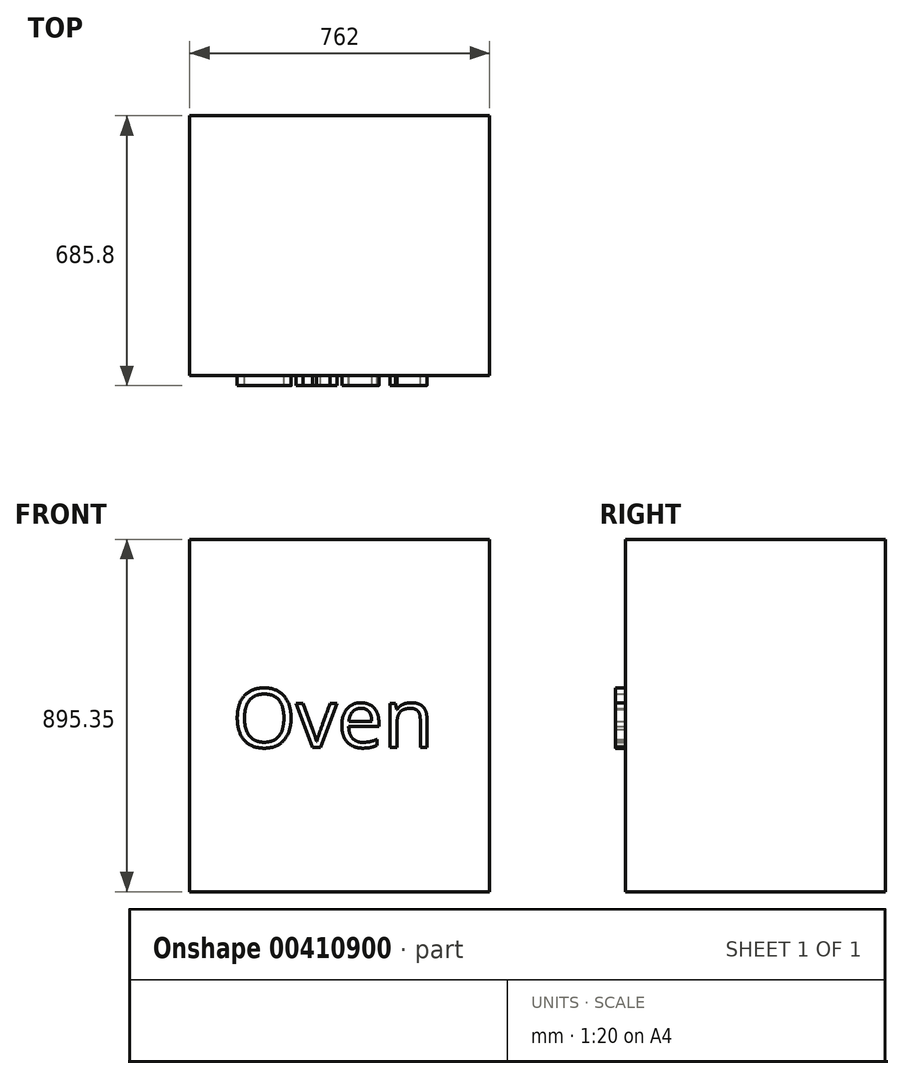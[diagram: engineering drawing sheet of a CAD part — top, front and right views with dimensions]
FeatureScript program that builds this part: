
annotation { "Feature Type Name" : "Feature", "Feature Type Description" : "" }
export const myFeature = defineFeature(function(context is Context, id is Id, definition is map)
    precondition{}
    {
        {
            var Q0;
            Q0=qCreatedBy(makeId("Front.planeOp"),FACE);
            var sketch = newSketch(context, id + "F0", { "sketchPlane" : qUnion([Q0])});
            skLineSegment(sketch, "E0.bottom", {"start": v(-762, 895.35) * mm, "end": v(0, 895.35) * mm});
            skLineSegment(sketch, "E0.top", {"start": v(-762, 0) * mm, "end": v(0, 0) * mm});
            skLineSegment(sketch, "E0.left", {"start": v(-762, 895.35) * mm, "end": v(-762, 0) * mm});
            skLineSegment(sketch, "E0.right", {"start": v(0, 895.35) * mm, "end": v(0, 0) * mm});
            skSolve(sketch);
        }
        {
            var Q0;
            Q0=makeQuery(id+"F0.imprint","IMPRINT",FACE,{"disambiguationData":[TD([[makeQuery(id+"F0.imprint","IMPRINT",EDGE,{"derivedFrom":sQuery(id+"F0.wireOp",EDGE,"E0.bottom")}),-1.0]])]});
            extrude(context, id + "F1", {"entities" : qUnion([Q0]), "depth" : 660.4 * mm});
        }
        {
            var Q0;
            Q0=makeQuery(id+"F1.opExtrude","CAP_FACE",FACE,{"disambiguationData":[OSD([sQuery(id+"F0.wireOp",EDGE,"E0.bottom"),sQuery(id+"F0.wireOp",EDGE,"E0.top"),sQuery(id+"F0.wireOp",EDGE,"E0.left"),sQuery(id+"F0.wireOp",EDGE,"E0.right")])],"isStart":false});
            var sketch = newSketch(context, id + "F2", { "sketchPlane" : qUnion([Q0])});
            skText(sketch, "E1", { "text": "Oven", "fontName": "OpenSans-Regular.ttf"});
            const initialGuessF2  = {"E1": [-0.65413, 0.3666, 1, 0, 0.14997]};
            skSetInitialGuess(sketch, initialGuessF2);
            skSolve(sketch);
        }
        {
            var Q0;
            Q0 = qSketchRegion(id + "F2", true);
            extrude(context, id + "F3", {"entities" : qUnion([Q0]), "operationType" : NewBodyOperationType.ADD, "depth" : 25.4 * mm});
        }
    });
